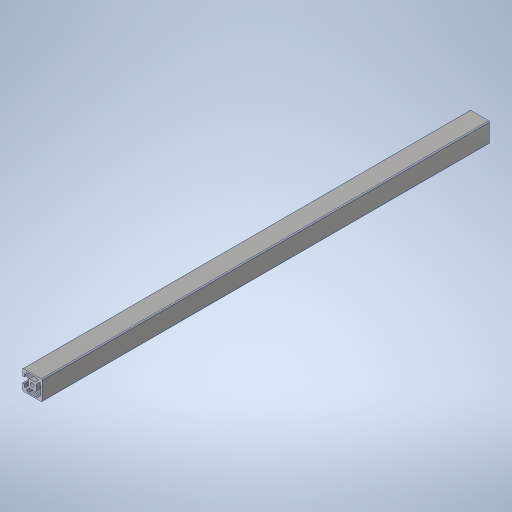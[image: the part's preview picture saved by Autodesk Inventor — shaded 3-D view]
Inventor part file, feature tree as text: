
AUTODESK INVENTOR PART (.ipt)
format: ipt  version: 2024 (Build 280153000, 153)  size: 353,792 bytes
history: native  units: mm
features: other x7, thread x2, sketch x2, extrude x1, hole x1
ambient origin geometry x8: Origin, YZ Plane, XZ Plane, XY Plane, X Axis, Y Axis, Z Axis, Center Point
bodies: Solid1 (feature_tree)
feature tree (13):
  extrude  "Extrusion1"  TaperAngle=0.0deg  [1 undecoded]
  hole  "Hole1"  [1 undecoded]
  other  "C1_XY"
  other  "C1_YZ"
  other  "C1_ZX"
  other  "C1_X"
  other  "C1_Y"
  other  "C1_Z"
  other  "C1_Center"
  thread  "Thread1"  [1 undecoded]
  thread  "Thread2"  [1 undecoded]
  sketch  "Sketch_66"  dims[d2=4.2mm d3=6.0mm d4=4.0mm d5=2.0mm d6=90.0deg d7=390.0mm d8=0.0mm d9=0.0mm d10=10.0mm d11=0.0mm d12=10.0mm d13=0.0mm]
  sketch  "Sketch2"  dims[d0=450.0mm d1=0.0mm]
note: 4 required parameter values undecoded (feature->parameter linkage not recoverable at this tier; creation-order binding heuristic only, values carry confidence <= 0.55)
